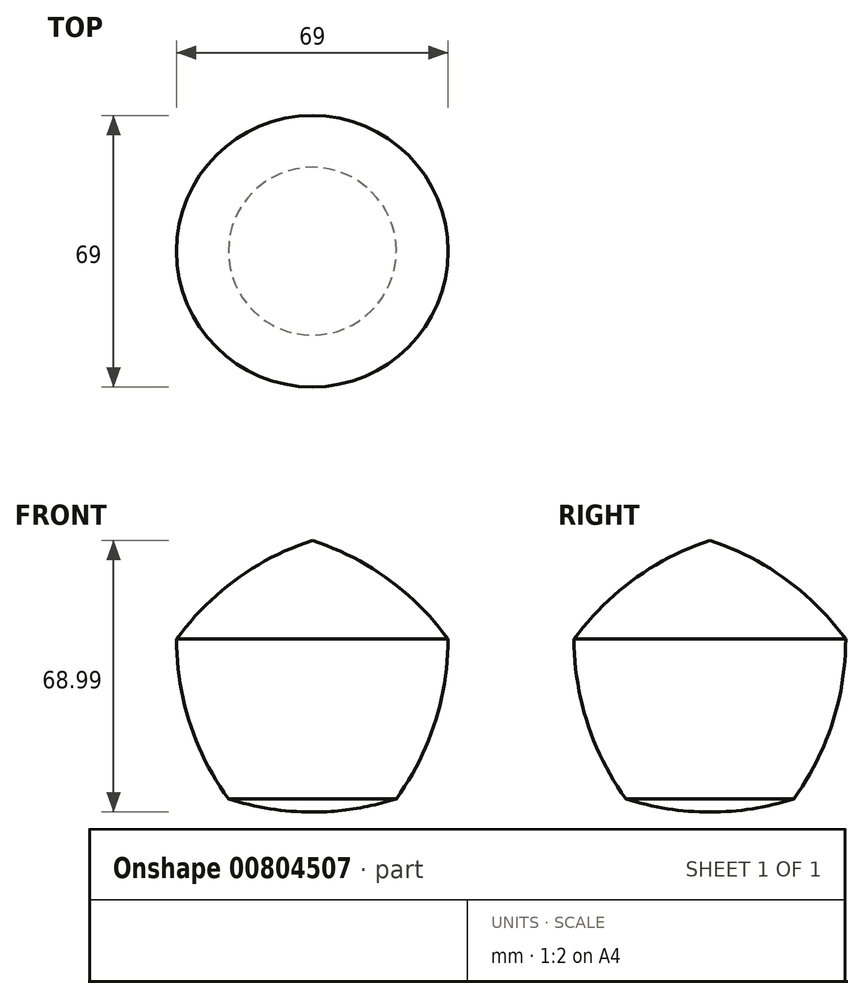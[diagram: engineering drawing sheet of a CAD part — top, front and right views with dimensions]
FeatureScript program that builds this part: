
annotation { "Feature Type Name" : "Feature", "Feature Type Description" : "" }
export const myFeature = defineFeature(function(context is Context, id is Id, definition is map)
    precondition{}
    {
        {
            var Q0;
            Q0=qCreatedBy(makeId("Front.planeOp"),FACE);
            var sketch = newSketch(context, id + "F0", { "sketchPlane" : qUnion([Q0])});
            skCircle(sketch, "E0.cCircle", {"center": v(0, 0) * mm, "radius": 29.35 * mm, "construction": true});
            skLineSegment(sketch, "E0.0", {"start": v(21.32, -29.35) * mm, "end": v(-21.32, -29.35) * mm});
            skLineSegment(sketch, "E0.1", {"start": v(-21.32, -29.35) * mm, "end": v(-34.5, 11.2) * mm});
            skLineSegment(sketch, "E0.2", {"start": v(-34.5, 11.2) * mm, "end": v(0, 36.27) * mm});
            skLineSegment(sketch, "E0.3", {"start": v(0, 36.27) * mm, "end": v(34.5, 11.2) * mm});
            skLineSegment(sketch, "E0.4", {"start": v(34.5, 11.2) * mm, "end": v(21.32, -29.35) * mm});
            skPoint(sketch, "E0.0.midPoint", {"position": v(0, -29.35) * mm});
            skCircle(sketch, "E1", {"center": v(-34.5, 11.2) * mm, "radius": 69 * mm});
            skCircle(sketch, "E2", {"center": v(34.5, 11.2) * mm, "radius": 69 * mm});
            skCircle(sketch, "E3", {"center": v(0, 36.27) * mm, "radius": 69 * mm});
            skCircle(sketch, "E4", {"center": v(-21.32, -29.35) * mm, "radius": 69 * mm});
            skCircle(sketch, "E5", {"center": v(21.32, -29.35) * mm, "radius": 69 * mm});
            skLineSegment(sketch, "E6", {"start": v(0, 36.27) * mm, "end": v(0, -35.19) * mm});
            skSolve(sketch);
        }
        {
            var Q0;
            {var subQ4=sQuery(id+"F0.wireOp",EDGE,"E0.3");Q0=makeQuery(id+"F0.imprint","IMPRINT",FACE,{"disambiguationData":[TD([[makeQuery(id+"F0.imprint","IMPRINT",EDGE,{"derivedFrom":subQ4}),-1.0]])]});}
            var Q1;
            {var subQ0=sQuery(id+"F0.wireOp",EDGE,"E0.3");Q1=makeQuery(id+"F0.imprint","IMPRINT",FACE,{"disambiguationData":[TD([[makeQuery(id+"F0.imprint","IMPRINT",EDGE,{"derivedFrom":subQ0}),1.0]])]});}
            var Q2;
            {var subQ0=sQuery(id+"F0.wireOp",EDGE,"E0.4");Q2=makeQuery(id+"F0.imprint","IMPRINT",FACE,{"disambiguationData":[TD([[makeQuery(id+"F0.imprint","IMPRINT",EDGE,{"derivedFrom":subQ0}),1.0]])]});}
            var Q3;
            {var subQ0=sQuery(id+"F0.wireOp",EDGE,"E3");var subQ3=sQuery(id+"F0.wireOp",EDGE,"E6");var subQ5=makeQuery(id+"F0.imprint","INTERSECT",VERTEX,{"derivedFrom":[subQ0,subQ3]});Q3=makeQuery(id+"F0.imprint","IMPRINT",FACE,{"disambiguationData":[TD([[makeQuery(id+"F0.imprint","IMPRINT",EDGE,{"disambiguationData":[TD([[subQ5,1.0]])],"derivedFrom":subQ3}),1.0]])]});}
            var Q4;
            Q4=sQuery(id+"F0.wireOp",EDGE,"E6");
            revolve(context, id + "F1", {"surfaceOperationType" : NewSurfaceOperationType.NEW, "entities" : qUnion([Q0, Q1, Q2, Q3]), "axis" : qUnion([Q4]), "revolveType" : RevolveType.FULL});
        }
    });
